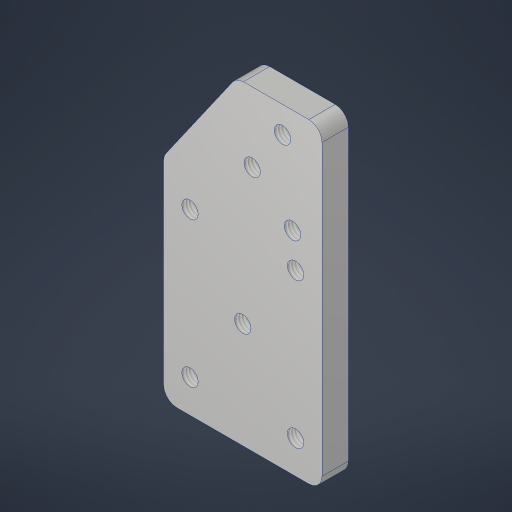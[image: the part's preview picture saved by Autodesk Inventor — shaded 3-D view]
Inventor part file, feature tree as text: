
AUTODESK INVENTOR PART (.ipt)
format: ipt  version: 2023.4 (Build 274418000, 418)  size: 240,640 bytes
history: native  units: in
note: dims shown in document units (in); Inventor stores cm internally (conversion verified against a paired STEP export)
features: sketch x1, extrude x1, hole x1, fillet x1
ambient origin geometry x8: Origin, YZ Plane, XZ Plane, XY Plane, X Axis, Y Axis, Z Axis, Center Point
bodies: Solid1 (feature_tree)
feature tree (4):
  sketch  "Sketch1"  dims[d0=2.0in d1=14.0in d2=0.3779in d3=1.0in d4=2.0in d5=15.25in d6=17.0in d10=0.5in d11=0.3125in d12=1.0in d13=0.3125in d14=5.9055in d16=1.0in d17=0.3937in d19=1.0in d21=1.375in d22=1.25in d23=1.25in d24=1.25in d25=4.75in d26=1.25in d27=3.0in d28=0.75in d29=1.5748in d31=0.5in d32=0.3937in d34=1.0in d37=0.25in d38=0.25in d39=0.25in d40=0.201in d41=0.25in d42=0.0in d43=0.156in d44=0.38in d45=0.375in d46=0.25in d47=0.5635in d48=1.0in d49=0.8108in d50=0.125in]
  extrude  "Extrusion1"  Depth=0.125in
  hole  "Hole1"  [1 undecoded]
  fillet  "Fillet1"  Radius=1.0in
note: 1 required parameter value undecoded (feature->parameter linkage not recoverable at this tier; creation-order binding heuristic only, values carry confidence <= 0.55)
